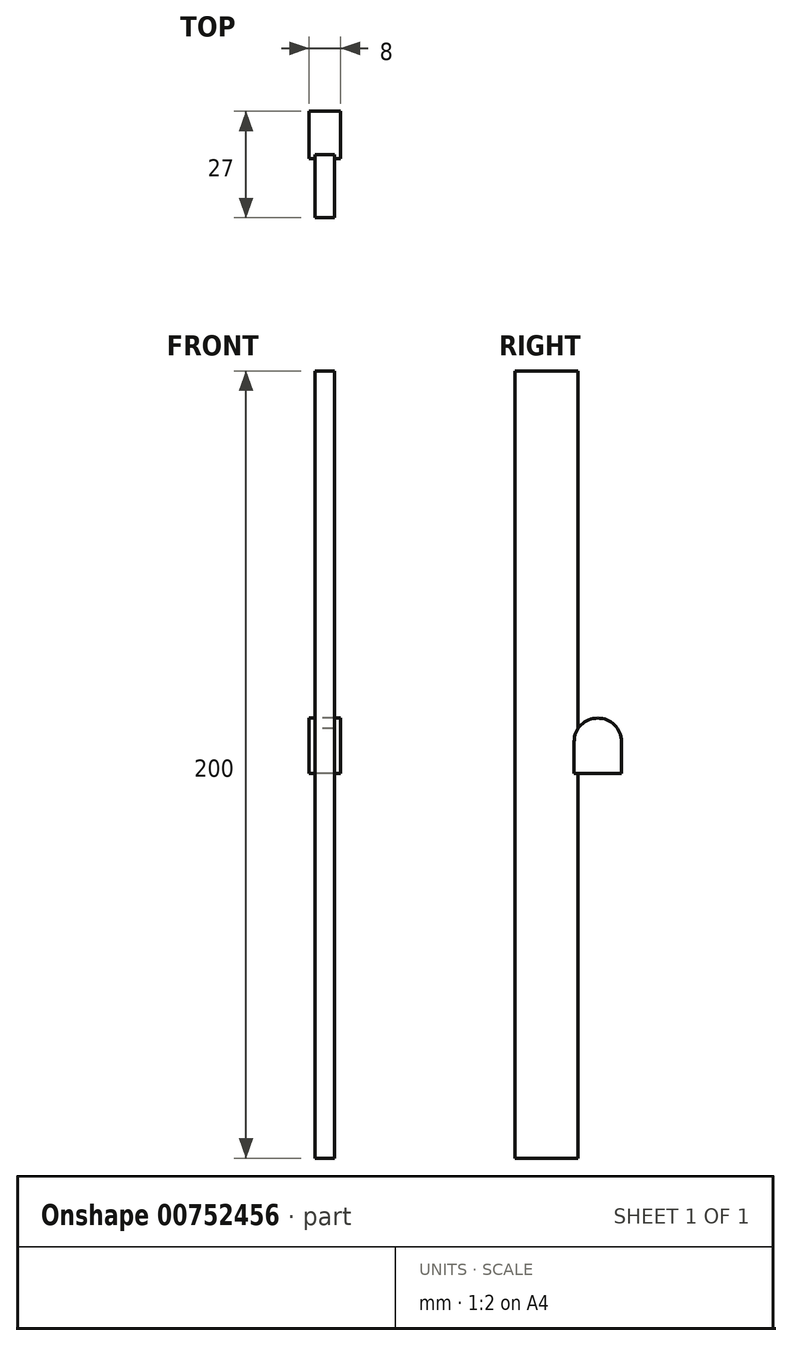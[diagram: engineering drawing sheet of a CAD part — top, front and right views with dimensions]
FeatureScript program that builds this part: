
annotation { "Feature Type Name" : "Feature", "Feature Type Description" : "" }
export const myFeature = defineFeature(function(context is Context, id is Id, definition is map)
    precondition{}
    {
        {
            var Q0;
            Q0=qCreatedBy(makeId("Right.planeOp"),FACE);
            var sketch = newSketch(context, id + "F0", { "sketchPlane" : qUnion([Q0])});
            skLineSegment(sketch, "E0.bottom", {"start": v(-27, 102.17) * mm, "end": v(-11, 102.17) * mm});
            skLineSegment(sketch, "E0.top", {"start": v(-27, -97.83) * mm, "end": v(-11, -97.83) * mm});
            skLineSegment(sketch, "E0.left", {"start": v(-27, 102.17) * mm, "end": v(-27, -97.83) * mm});
            skLineSegment(sketch, "E0.right", {"start": v(-11, 102.17) * mm, "end": v(-11, -97.83) * mm});
            skLineSegment(sketch, "E1", {"start": v(0, 0) * mm, "end": v(-12, 0) * mm});
            skLineSegment(sketch, "E2", {"start": v(0, 8) * mm, "end": v(0, 0) * mm});
            skLineSegment(sketch, "E3", {"start": v(-12, 8) * mm, "end": v(-12, 0) * mm});
            skArc(sketch, "E4", {"start": v(0, 8) * mm, "mid": v(-6, 14) * mm, "end": v(-12, 8) * mm});
            skSolve(sketch);
        }
        {
            var Q0;
            {var subQ0=sQuery(id+"F0.wireOp",EDGE,"E0.bottom");Q0=makeQuery(id+"F0.imprint","IMPRINT",FACE,{"disambiguationData":[TD([[makeQuery(id+"F0.imprint","IMPRINT",EDGE,{"derivedFrom":subQ0}),-1.0]])]});}
            var Q1;
            {var subQ1=sQuery(id+"F0.wireOp",EDGE,"E0.top");Q1=makeQuery(id+"F0.imprint","IMPRINT",FACE,{"disambiguationData":[TD([[makeQuery(id+"F0.imprint","IMPRINT",EDGE,{"derivedFrom":subQ1}),1.0]])]});}
            var Q2;
            {var subQ0=sQuery(id+"F0.wireOp",EDGE,"d5ezwpda-OrtV-Myah-qhd7-Szyf6rVC7jLu");var subQ1=sQuery(id+"F0.wireOp",EDGE,"E0.right");var subQ2=makeQuery(id+"F0.imprint","INTERSECT",VERTEX,{"disambiguationData":[OD(0.0)],"derivedFrom":[subQ1,subQ0]});Q2=makeQuery(id+"F0.imprint","IMPRINT",FACE,{"disambiguationData":[TD([[makeQuery(id+"F0.imprint","IMPRINT",EDGE,{"disambiguationData":[TD([[subQ2,1.0]])],"derivedFrom":subQ1}),-1.0]])]});}
            var Q3;
            {var subQ5=sQuery(id+"F0.wireOp",EDGE,"E3");Q3=makeQuery(id+"F0.imprint","IMPRINT",FACE,{"disambiguationData":[TD([[makeQuery(id+"F0.imprint","IMPRINT",EDGE,{"derivedFrom":subQ5}),1.0]])]});}
            extrude(context, id + "F1", {"entities" : qUnion([Q0, Q1, Q2, Q3]), "endBound" : BoundingType.SYMMETRIC, "depth" : 5 * mm, "offsetDistance" : 25 * mm});
        }
        {
            var Q0;
            {var subQ5=sQuery(id+"F0.wireOp",EDGE,"E2");Q0=makeQuery(id+"F0.imprint","IMPRINT",FACE,{"disambiguationData":[TD([[makeQuery(id+"F0.imprint","IMPRINT",EDGE,{"derivedFrom":subQ5}),-1.0]])]});}
            var Q1;
            {var subQ5=sQuery(id+"F0.wireOp",EDGE,"E3");Q1=makeQuery(id+"F0.imprint","IMPRINT",FACE,{"disambiguationData":[TD([[makeQuery(id+"F0.imprint","IMPRINT",EDGE,{"derivedFrom":subQ5}),1.0]])]});}
            extrude(context, id + "F2", {"entities" : qUnion([Q0, Q1]), "operationType" : NewBodyOperationType.ADD, "endBound" : BoundingType.SYMMETRIC, "depth" : 8 * mm, "offsetDistance" : 25 * mm});
        }
    });
